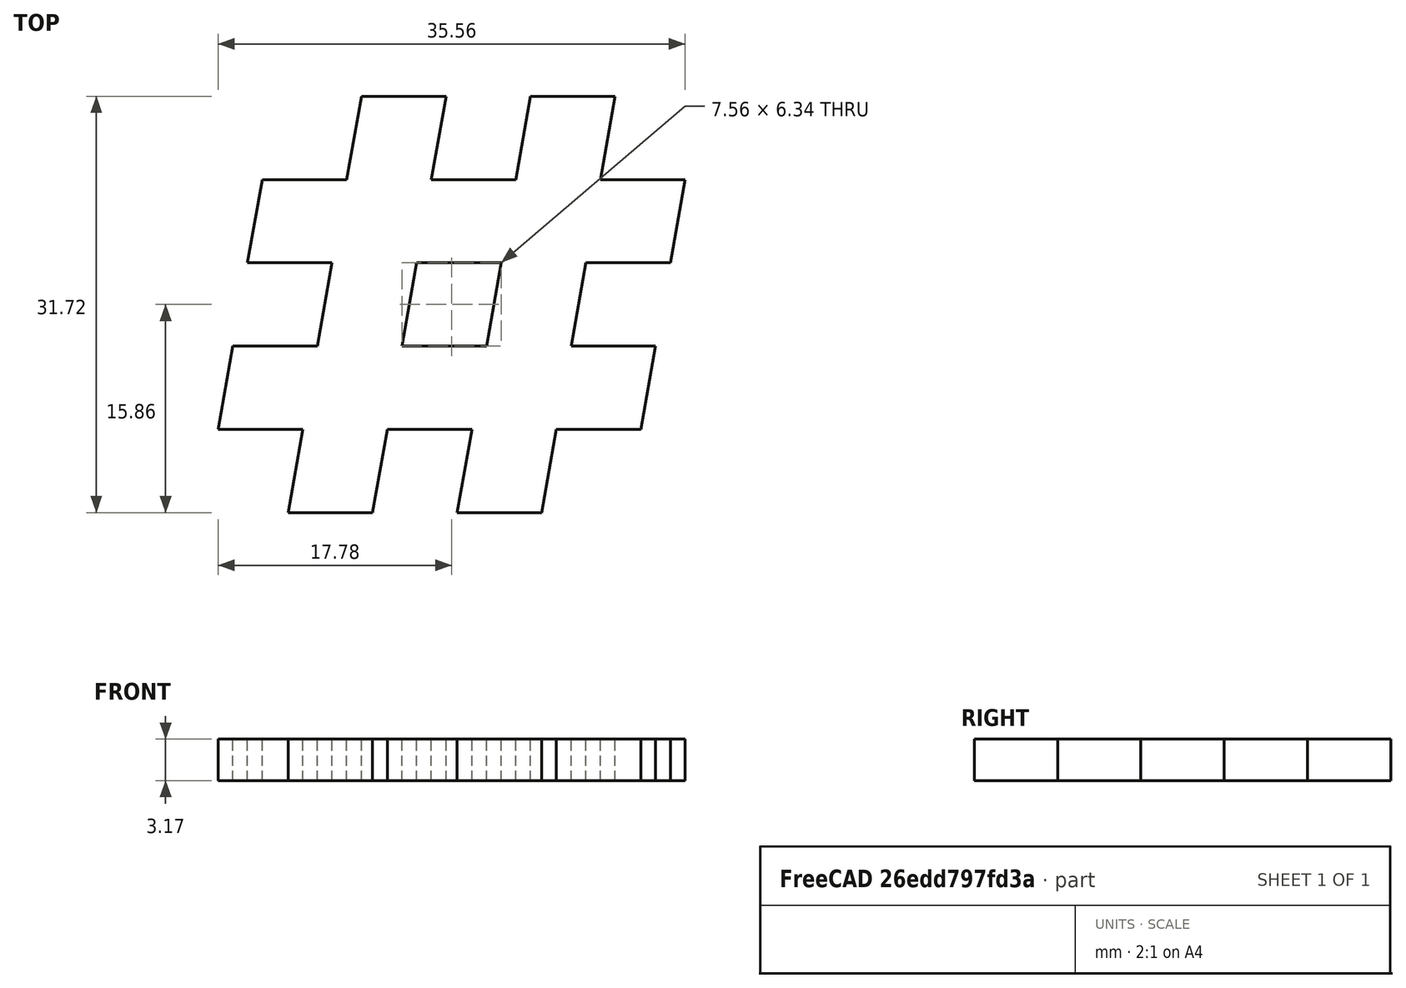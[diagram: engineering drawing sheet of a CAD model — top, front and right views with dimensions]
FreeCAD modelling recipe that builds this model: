
FCSTD DOCUMENT  (FreeCAD 0.20R26651 (Git))
Label: Media_Template
License: All rights reserved
LicenseURL: http://en.wikipedia.org/wiki/All_rights_reserved
objects: TechDraw::DrawViewDimExtent×2, Sketcher::SketchObject×1, PartDesign::Pad×1, PartDesign::Body×1, TechDraw::DrawSVGTemplate×1, TechDraw::DrawProjGroupItem×1, TechDraw::DrawProjGroup×1, TechDraw::DrawViewDimension×1, TechDraw::DrawViewAnnotation×1, TechDraw::DrawPage×1
note: 4 computed .brp shape members not serialized (recipe doc carries the construction recipe); baked Part::Feature solids carry a one-line shape summary decoded from their .brp

FEATURE [Sketcher::SketchObject] Sketch
  FullyConstrained = true
  MapMode = 5
  Support = -> [XY_Plane]
  sketch-geometry (32):
    g0: LineSegment StartX=-14.4246 StartY=9.51461 StartZ=0 EndX=-15.5431 EndY=3.17154 EndZ=0
    g1: LineSegment StartX=-16.6615 StartY=-3.17154 StartZ=0 EndX=-17.78 EndY=-9.51461 EndZ=0
    g2: LineSegment StartX=-14.4246 StartY=9.51461 StartZ=0 EndX=-7.98371 EndY=9.51461 EndZ=0
    g3: LineSegment StartX=-15.5431 StartY=3.17154 StartZ=0 EndX=-9.10216 EndY=3.17154 EndZ=0
    g4: LineSegment StartX=-9.10216 StartY=3.17154 StartZ=0 EndX=-10.2206 EndY=-3.17154 EndZ=0
    g5: LineSegment StartX=-10.2206 StartY=-3.17154 StartZ=0 EndX=-16.6615 EndY=-3.17154 EndZ=0
    g6: LineSegment StartX=-17.78 StartY=-9.51461 StartZ=0 EndX=-11.3391 EndY=-9.51461 EndZ=0
    g7: LineSegment StartX=-11.3391 StartY=-9.51461 StartZ=0 EndX=-12.4575 EndY=-15.8577 EndZ=0
    g8: LineSegment StartX=-12.4575 StartY=-15.8577 StartZ=0 EndX=-6.0166 EndY=-15.8577 EndZ=0
    g9: LineSegment StartX=-6.0166 StartY=-15.8577 StartZ=0 EndX=-4.89815 EndY=-9.51461 EndZ=0
    g10: LineSegment StartX=-4.89815 StartY=-9.51461 StartZ=0 EndX=1.54278 EndY=-9.51461 EndZ=0
    g11: LineSegment StartX=1.54278 StartY=-9.51461 StartZ=0 EndX=0.424325 EndY=-15.8577 EndZ=0
    g12: LineSegment StartX=0.424325 StartY=-15.8577 StartZ=0 EndX=6.86525 EndY=-15.8577 EndZ=0
    g13: LineSegment StartX=6.86525 StartY=-15.8577 StartZ=0 EndX=7.98371 EndY=-9.51461 EndZ=0
    g14: LineSegment StartX=7.98371 StartY=-9.51461 StartZ=0 EndX=14.4246 EndY=-9.51461 EndZ=0
    g15: LineSegment StartX=14.4246 StartY=-9.51461 StartZ=0 EndX=15.5431 EndY=-3.17154 EndZ=0
    g16: LineSegment StartX=15.5431 StartY=-3.17154 StartZ=0 EndX=9.10216 EndY=-3.17154 EndZ=0
    g17: LineSegment StartX=9.10216 StartY=-3.17154 StartZ=0 EndX=10.2206 EndY=3.17154 EndZ=0
    g18: LineSegment StartX=10.2206 StartY=3.17154 StartZ=0 EndX=16.6615 EndY=3.17154 EndZ=0
    g19: LineSegment StartX=16.6615 StartY=3.17154 StartZ=0 EndX=17.78 EndY=9.51461 EndZ=0
    g20: LineSegment StartX=17.78 StartY=9.51461 StartZ=0 EndX=11.3391 EndY=9.51461 EndZ=0
    g21: LineSegment StartX=11.3391 StartY=9.51461 StartZ=0 EndX=12.4575 EndY=15.8577 EndZ=0
    g22: LineSegment StartX=12.4575 StartY=15.8577 StartZ=0 EndX=6.0166 EndY=15.8577 EndZ=0
    g23: LineSegment StartX=6.0166 StartY=15.8577 StartZ=0 EndX=4.89815 EndY=9.51461 EndZ=0
    g24: LineSegment StartX=4.89815 StartY=9.51461 StartZ=0 EndX=-1.54278 EndY=9.51461 EndZ=0
    g25: LineSegment StartX=-1.54278 StartY=9.51461 StartZ=0 EndX=-0.424325 EndY=15.8577 EndZ=0
    g26: LineSegment StartX=-0.424325 StartY=15.8577 StartZ=0 EndX=-6.86525 EndY=15.8577 EndZ=0
    g27: LineSegment StartX=-6.86525 StartY=15.8577 StartZ=0 EndX=-7.98371 EndY=9.51461 EndZ=0
    g28: LineSegment StartX=-2.66124 StartY=3.17154 StartZ=0 EndX=-3.77969 EndY=-3.17154 EndZ=0
    g29: LineSegment StartX=-3.77969 StartY=-3.17154 StartZ=0 EndX=2.66124 EndY=-3.17154 EndZ=0
    g30: LineSegment StartX=2.66124 StartY=-3.17154 StartZ=0 EndX=3.77969 EndY=3.17154 EndZ=0
    g31: LineSegment StartX=3.77969 StartY=3.17154 StartZ=0 EndX=-2.66124 EndY=3.17154 EndZ=0
  constraints (75):
    c: Coincident(g2,g0)
    c: Horizontal(g2)
    c: Coincident(g0,g3)
    c: Horizontal(g3)
    c: Coincident(g3,g4)
    c: Coincident(g4,g5)
    c: Coincident(g5,g1)
    c: Coincident(g1,g6)
    c: Coincident(g6,g7)
    c: Coincident(g7,g8)
    c: Coincident(g8,g9)
    c: Coincident(g9,g10)
    c: Horizontal(g10)
    c: Coincident(g10,g11)
    c: Coincident(g11,g12)
    c: Horizontal(g12)
    c: Coincident(g12,g13)
    c: Coincident(g13,g14)
    c: Coincident(g14,g15)
    c: Coincident(g15,g16)
    c: Coincident(g16,g17)
    c: Coincident(g17,g18)
    c: Coincident(g18,g19)
    c: Coincident(g19,g20)
    c: Coincident(g20,g21)
    c: Coincident(g21,g22)
    c: Coincident(g22,g23)
    c: Coincident(g23,g24)
    c: Coincident(g24,g25)
    c: Coincident(g25,g26)
    c: Horizontal(g26)
    c: Coincident(g26,g27)
    c: Coincident(g27,g2)
    c: Horizontal(g5)
    c: Tangent(g10,g6)
    c: Tangent(g10,g14)
    c: Tangent(g24,g2)
    c: Tangent(g24,g20)
    c: Tangent(g3,g18)
    c: Tangent(g5,g16)
    c: Tangent(g9,g25)
    c: Tangent(g11,g23)
    c: Tangent(g13,g21)
    c: Tangent(g7,g27)
    c: Parallel(g19,g0)
    c: Parallel(g0,g27)
    c: Parallel(g25,g23)
    c: Parallel(g21,g23)
    c: Parallel(g27,g21)
    c: Tangent(g4,g27)
    c: Tangent(g26,g22)
    c: Tangent(g19,g15)
    c: Tangent(g21,g17)
    c: Tangent(g12,g8)
    c: Tangent(g1,g0)
    c: Equal(g2,g27)
    c: Equal(g27,g26)
    c: Equal(g26,g24)
    c: Equal(g22,g23)
    c: Equal(g20,g21)
    c: Equal(g20,g19)
    c: Equal(g18,g17)
    c: Equal(g5,g1)
    c: Equal(g7,g1)
    c: Symmetric(g3,g16,g-1)
    c: Angle(g24,g25) = 1.39626
    c: Coincident(g29,g28)
    c: Coincident(g30,g29)
    c: Coincident(g31,g30)
    c: Coincident(g31,g28)
    c: Tangent(g18,g31)
    c: Tangent(g30,g23)
    c: Tangent(g28,g25)
    c: Tangent(g29,g5)
    c: DistanceX(g1,g19) = 35.56
FEATURE [PartDesign::Pad] Pad
  Direction = (0,0,1)
  Length = 3.175
  Length2 = 100.076
  Profile = -> Sketch
  ReferenceAxis = -> Sketch [N_Axis]
  Type = 0
FEATURE [PartDesign::Body] Body  label="Media Template Body"
  Group = -> [Sketch,Pad]
  Origin = -> Origin
  Tip = -> Pad
FEATURE [TechDraw::DrawSVGTemplate] Template
  EditableTexts = Designed_by_Name=Design by Matthew; Drawing_number=30c5bd87; FC-Date=Dec 2021; FC-SC=1:1; FC-SH=1 of 1; FC-Title=Media Subteam Patch; Subtitle=Tidal Force Robotics; Weight=0.01
  Height = 210
  Orientation = 1
  Width = 297
FEATURE [TechDraw::DrawProjGroupItem] ProjItem  label="Front"
  CoarseView = false
  Direction = (0,0,1)
  Focus = 100
  HardHidden = false
  IsoCount = 0
  IsoHidden = false
  IsoVisible = false
  LockPosition = true
  Perspective = false
  Rotation = 0
  RotationVector = (1,0,0)
  ScaleType = 2
  SeamHidden = false
  SeamVisible = true
  SmoothHidden = false
  SmoothVisible = true
  Source = -> [Body]
  Type = 0
  X = 0
  XDirection = (1,0,0)
  Y = 0
FEATURE [TechDraw::DrawProjGroup] ProjGroup
  Anchor = -> ProjItem
  AutoDistribute = true
  LockPosition = false
  ProjectionType = 0
  Rotation = 0
  ScaleType = 0
  Source = -> [Body]
  Views = -> [ProjItem]
  X = 148.5
  Y = 105
  spacingX = 14.986
  spacingY = 14.986
FEATURE [TechDraw::DrawViewDimExtent] DimExtent
  Arbitrary = false
  ArbitraryTolerances = false
  CosmeticTags = 4876a07e-5734-4a42-9c70-3ad1e6a7d9bc | d5695a1d-5df9-4573-af45-24d7c8faea45
  DirExtent = 0
  EqualTolerance = true
  FormatSpec = %.3f
  FormatSpecOverTolerance = %+.3f
  FormatSpecUnderTolerance = %+.3f
  Inverted = false
  LockPosition = false
  MeasureType = 1
  OverTolerance = 0
  References2D = -> [ProjItem]
  Rotation = 0
  ScaleType = 0
  Source = -> [ProjItem]
  TheoreticalExact = false
  Type = 1
  UnderTolerance = 0
  X = 0.802663
  Y = -28.3225
FEATURE [TechDraw::DrawViewDimExtent] DimExtent001
  Arbitrary = false
  ArbitraryTolerances = false
  CosmeticTags = cb7f4163-6724-4b0a-a852-f6ca696e9f43 | 79479888-a2d5-4abe-9f57-d4747772a0c1
  DirExtent = 1
  EqualTolerance = true
  FormatSpec = %.3f
  FormatSpecOverTolerance = %+.3f
  FormatSpecUnderTolerance = %+.3f
  Inverted = false
  LockPosition = false
  MeasureType = 1
  OverTolerance = 0
  References2D = -> [ProjItem]
  Rotation = 0
  ScaleType = 0
  Source = -> [ProjItem]
  TheoreticalExact = false
  Type = 2
  UnderTolerance = 0
  X = 31.3039
  Y = 1.83466
FEATURE [TechDraw::DrawViewDimension] Dimension
  Arbitrary = false
  ArbitraryTolerances = false
  EqualTolerance = true
  FormatSpec = %.3f
  FormatSpecOverTolerance = %+.3f
  FormatSpecUnderTolerance = %+.3f
  Inverted = false
  LockPosition = false
  MeasureType = 1
  OverTolerance = 0
  References2D = -> [ProjItem]
  Rotation = 0
  ScaleType = 0
  TheoreticalExact = false
  Type = 1
  UnderTolerance = 0
  X = -40.0702
  Y = -3.02243
FEATURE [TechDraw::DrawViewAnnotation] Annotation
  Font = osifont
  LineSpace = 80
  LockPosition = false
  MaxWidth = -1
  Rotation = 0
  ScaleType = 0
  Text = All line segments same length
  TextSize = 5.08
  TextStyle = 0
  X = 92.6236
  Y = 87.1671
FEATURE [TechDraw::DrawPage] Page
  KeepUpdated = true
  NextBalloonIndex = 1
  ProjectionType = 0
  Template = -> Template
  Views = -> [ProjGroup,DimExtent,DimExtent001,Dimension,Annotation]
